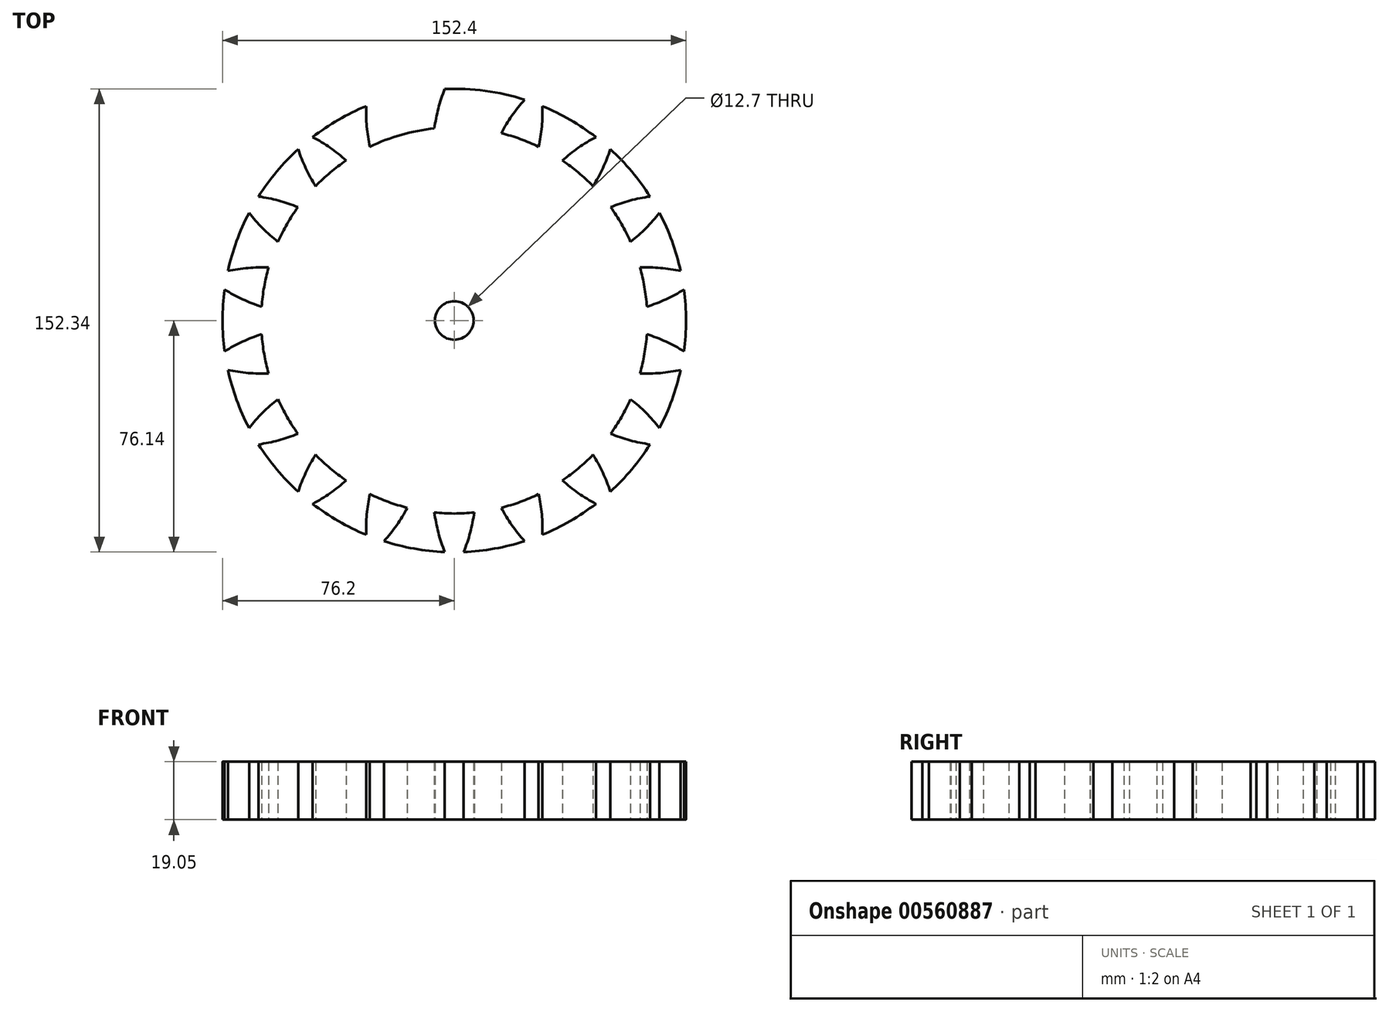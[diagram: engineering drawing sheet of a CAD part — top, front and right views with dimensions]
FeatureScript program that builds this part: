
annotation { "Feature Type Name" : "Feature", "Feature Type Description" : "" }
export const myFeature = defineFeature(function(context is Context, id is Id, definition is map)
    precondition{}
    {
        {
            var Q0;
            Q0=qCreatedBy(makeId("Top.planeOp"),FACE);
            var sketch = newSketch(context, id + "F0", { "sketchPlane" : qUnion([Q0])});
            skCircle(sketch, "E0", {"center": v(0, 0) * mm, "radius": 63.5 * mm});
            skLineSegment(sketch, "E1", {"start": v(0, 0) * mm, "end": v(-81.9, 97.6) * mm, "construction": true});
            skCircle(sketch, "E2", {"center": v(-46.94, 55.94) * mm, "radius": 53.98 * mm, "construction": true});
            skCircle(sketch, "E3", {"center": v(0, 0) * mm, "radius": 76.2 * mm});
            skArc(sketch, "E4", {"start": v(6.55, 63.16) * mm, "mid": v(5.24, 69.76) * mm, "end": v(3.11, 76.14) * mm});
            skArc(sketch, "E5.MirrorCS", {"start": v(-6.55, 63.16) * mm, "mid": v(-5.24, 69.76) * mm, "end": v(-3.11, 76.14) * mm});
            skArc(sketch, "E6", {"start": v(-3.11, 76.14) * mm, "mid": v(0, 76.2) * mm, "end": v(3.11, 76.14) * mm});
            skArc(sketch, "E7.1.0", {"start": v(15.45, 61.6) * mm, "mid": v(18.94, 67.34) * mm, "end": v(23.11, 72.61) * mm});
            skArc(sketch, "E7.1.1", {"start": v(27.76, 57.11) * mm, "mid": v(28.78, 63.76) * mm, "end": v(28.97, 70.48) * mm});
            skArc(sketch, "E7.1.2", {"start": v(23.11, 72.61) * mm, "mid": v(26.06, 71.6) * mm, "end": v(28.97, 70.48) * mm});
            skArc(sketch, "E7.2.0", {"start": v(35.58, 52.6) * mm, "mid": v(40.83, 56.8) * mm, "end": v(46.55, 60.33) * mm});
            skArc(sketch, "E7.2.1", {"start": v(45.62, 44.17) * mm, "mid": v(48.85, 50.07) * mm, "end": v(51.33, 56.32) * mm});
            skArc(sketch, "E7.2.2", {"start": v(46.55, 60.33) * mm, "mid": v(48.98, 58.37) * mm, "end": v(51.33, 56.32) * mm});
            skArc(sketch, "E7.3.0", {"start": v(51.42, 37.25) * mm, "mid": v(57.8, 39.41) * mm, "end": v(64.38, 40.77) * mm});
            skArc(sketch, "E7.3.1", {"start": v(57.97, 25.9) * mm, "mid": v(63.03, 30.34) * mm, "end": v(67.5, 35.37) * mm});
            skArc(sketch, "E7.3.2", {"start": v(64.38, 40.77) * mm, "mid": v(66, 38.1) * mm, "end": v(67.5, 35.37) * mm});
            skArc(sketch, "E7.4.0", {"start": v(61.06, 17.42) * mm, "mid": v(67.79, 17.27) * mm, "end": v(74.44, 16.29) * mm});
            skArc(sketch, "E7.4.1", {"start": v(63.34, 4.52) * mm, "mid": v(69.6, 6.96) * mm, "end": v(75.52, 10.15) * mm});
            skArc(sketch, "E7.4.2", {"start": v(74.44, 16.29) * mm, "mid": v(75.04, 13.23) * mm, "end": v(75.52, 10.15) * mm});
            skArc(sketch, "E7.5.0", {"start": v(63.34, -4.52) * mm, "mid": v(69.6, -6.96) * mm, "end": v(75.52, -10.15) * mm});
            skArc(sketch, "E7.5.1", {"start": v(61.06, -17.42) * mm, "mid": v(67.79, -17.27) * mm, "end": v(74.44, -16.29) * mm});
            skArc(sketch, "E7.5.2", {"start": v(75.52, -10.15) * mm, "mid": v(75.04, -13.23) * mm, "end": v(74.44, -16.29) * mm});
            skArc(sketch, "E7.6.0", {"start": v(57.97, -25.9) * mm, "mid": v(63.03, -30.34) * mm, "end": v(67.5, -35.37) * mm});
            skArc(sketch, "E7.6.1", {"start": v(51.42, -37.25) * mm, "mid": v(57.8, -39.41) * mm, "end": v(64.38, -40.77) * mm});
            skArc(sketch, "E7.6.2", {"start": v(67.5, -35.37) * mm, "mid": v(66, -38.1) * mm, "end": v(64.38, -40.77) * mm});
            skArc(sketch, "E7.7.0", {"start": v(45.62, -44.17) * mm, "mid": v(48.85, -50.07) * mm, "end": v(51.33, -56.32) * mm});
            skArc(sketch, "E7.7.1", {"start": v(35.58, -52.6) * mm, "mid": v(40.83, -56.8) * mm, "end": v(46.55, -60.33) * mm});
            skArc(sketch, "E7.7.2", {"start": v(51.33, -56.32) * mm, "mid": v(48.98, -58.37) * mm, "end": v(46.55, -60.33) * mm});
            skArc(sketch, "E7.8.0", {"start": v(27.76, -57.11) * mm, "mid": v(28.78, -63.76) * mm, "end": v(28.97, -70.48) * mm});
            skArc(sketch, "E7.8.1", {"start": v(15.45, -61.6) * mm, "mid": v(18.94, -67.34) * mm, "end": v(23.11, -72.61) * mm});
            skArc(sketch, "E7.8.2", {"start": v(28.97, -70.48) * mm, "mid": v(26.06, -71.6) * mm, "end": v(23.11, -72.61) * mm});
            skArc(sketch, "E7.9.0", {"start": v(6.55, -63.16) * mm, "mid": v(5.24, -69.76) * mm, "end": v(3.11, -76.14) * mm});
            skArc(sketch, "E7.9.1", {"start": v(-6.55, -63.16) * mm, "mid": v(-5.24, -69.76) * mm, "end": v(-3.11, -76.14) * mm});
            skArc(sketch, "E7.9.2", {"start": v(3.11, -76.14) * mm, "mid": v(0, -76.2) * mm, "end": v(-3.11, -76.14) * mm});
            skArc(sketch, "E7.10.0", {"start": v(-15.45, -61.6) * mm, "mid": v(-18.94, -67.34) * mm, "end": v(-23.11, -72.61) * mm});
            skArc(sketch, "E7.10.1", {"start": v(-27.76, -57.11) * mm, "mid": v(-28.78, -63.76) * mm, "end": v(-28.97, -70.48) * mm});
            skArc(sketch, "E7.10.2", {"start": v(-23.11, -72.61) * mm, "mid": v(-26.06, -71.6) * mm, "end": v(-28.97, -70.48) * mm});
            skArc(sketch, "E7.11.0", {"start": v(-35.58, -52.6) * mm, "mid": v(-40.83, -56.8) * mm, "end": v(-46.55, -60.33) * mm});
            skArc(sketch, "E7.11.1", {"start": v(-45.62, -44.17) * mm, "mid": v(-48.85, -50.07) * mm, "end": v(-51.33, -56.32) * mm});
            skArc(sketch, "E7.11.2", {"start": v(-46.55, -60.33) * mm, "mid": v(-48.98, -58.37) * mm, "end": v(-51.33, -56.32) * mm});
            skArc(sketch, "E7.12.0", {"start": v(-51.42, -37.25) * mm, "mid": v(-57.8, -39.41) * mm, "end": v(-64.38, -40.77) * mm});
            skArc(sketch, "E7.12.1", {"start": v(-57.97, -25.9) * mm, "mid": v(-63.03, -30.34) * mm, "end": v(-67.5, -35.37) * mm});
            skArc(sketch, "E7.12.2", {"start": v(-64.38, -40.77) * mm, "mid": v(-66, -38.1) * mm, "end": v(-67.5, -35.37) * mm});
            skArc(sketch, "E7.13.0", {"start": v(-61.06, -17.42) * mm, "mid": v(-67.79, -17.27) * mm, "end": v(-74.44, -16.29) * mm});
            skArc(sketch, "E7.13.1", {"start": v(-63.34, -4.52) * mm, "mid": v(-69.6, -6.96) * mm, "end": v(-75.52, -10.15) * mm});
            skArc(sketch, "E7.13.2", {"start": v(-74.44, -16.29) * mm, "mid": v(-75.04, -13.23) * mm, "end": v(-75.52, -10.15) * mm});
            skArc(sketch, "E7.14.0", {"start": v(-63.34, 4.52) * mm, "mid": v(-69.6, 6.96) * mm, "end": v(-75.52, 10.15) * mm});
            skArc(sketch, "E7.14.1", {"start": v(-61.06, 17.42) * mm, "mid": v(-67.79, 17.27) * mm, "end": v(-74.44, 16.29) * mm});
            skArc(sketch, "E7.14.2", {"start": v(-75.52, 10.15) * mm, "mid": v(-75.04, 13.23) * mm, "end": v(-74.44, 16.29) * mm});
            skArc(sketch, "E7.15.0", {"start": v(-57.97, 25.9) * mm, "mid": v(-63.03, 30.34) * mm, "end": v(-67.5, 35.37) * mm});
            skArc(sketch, "E7.15.1", {"start": v(-51.42, 37.25) * mm, "mid": v(-57.8, 39.41) * mm, "end": v(-64.38, 40.77) * mm});
            skArc(sketch, "E7.15.2", {"start": v(-67.5, 35.37) * mm, "mid": v(-66, 38.1) * mm, "end": v(-64.38, 40.77) * mm});
            skArc(sketch, "E7.16.0", {"start": v(-45.62, 44.17) * mm, "mid": v(-48.85, 50.07) * mm, "end": v(-51.33, 56.32) * mm});
            skArc(sketch, "E7.16.1", {"start": v(-35.58, 52.6) * mm, "mid": v(-40.83, 56.8) * mm, "end": v(-46.55, 60.33) * mm});
            skArc(sketch, "E7.16.2", {"start": v(-51.33, 56.32) * mm, "mid": v(-48.98, 58.37) * mm, "end": v(-46.55, 60.33) * mm});
            skArc(sketch, "E7.17.0", {"start": v(-27.76, 57.11) * mm, "mid": v(-28.78, 63.76) * mm, "end": v(-28.97, 70.48) * mm});
            skArc(sketch, "E7.17.1", {"start": v(-15.45, 61.6) * mm, "mid": v(-18.94, 67.34) * mm, "end": v(-23.11, 72.61) * mm});
            skArc(sketch, "E7.17.2", {"start": v(-28.97, 70.48) * mm, "mid": v(-26.06, 71.6) * mm, "end": v(-23.11, 72.61) * mm});
            skLineSegment(sketch, "E7.anchor1", {"start": v(0, 0) * mm, "end": v(-6.55, 63.16) * mm, "construction": true});
            skLineSegment(sketch, "E7.anchor2", {"start": v(0, 0) * mm, "end": v(-27.76, 57.11) * mm, "construction": true});
            skCircle(sketch, "E8", {"center": v(0, 0) * mm, "radius": 6.35 * mm});
            skSolve(sketch);
        }
        {
            var Q0;
            {var subQ0=sQuery(id+"F0.wireOp",EDGE,"E7.4.0");Q0=makeQuery(id+"F0.imprint","IMPRINT",FACE,{"disambiguationData":[TD([[makeQuery(id+"F0.imprint","IMPRINT",EDGE,{"derivedFrom":subQ0}),-1.0]])]});}
            var Q1;
            {var subQ0=sQuery(id+"F0.wireOp",EDGE,"E7.3.0");Q1=makeQuery(id+"F0.imprint","IMPRINT",FACE,{"disambiguationData":[TD([[makeQuery(id+"F0.imprint","IMPRINT",EDGE,{"derivedFrom":subQ0}),-1.0]])]});}
            var Q2;
            {var subQ0=sQuery(id+"F0.wireOp",EDGE,"E7.2.0");Q2=makeQuery(id+"F0.imprint","IMPRINT",FACE,{"disambiguationData":[TD([[makeQuery(id+"F0.imprint","IMPRINT",EDGE,{"derivedFrom":subQ0}),-1.0]])]});}
            var Q3;
            {var subQ0=sQuery(id+"F0.wireOp",EDGE,"E7.1.0");Q3=makeQuery(id+"F0.imprint","IMPRINT",FACE,{"disambiguationData":[TD([[makeQuery(id+"F0.imprint","IMPRINT",EDGE,{"derivedFrom":subQ0}),-1.0]])]});}
            var Q4;
            {var subQ0=sQuery(id+"F0.wireOp",EDGE,"E4");Q4=makeQuery(id+"F0.imprint","IMPRINT",FACE,{"disambiguationData":[TD([[makeQuery(id+"F0.imprint","IMPRINT",EDGE,{"derivedFrom":subQ0}),1.0]])]});}
            var Q5;
            {var subQ0=sQuery(id+"F0.wireOp",EDGE,"E7.17.0");Q5=makeQuery(id+"F0.imprint","IMPRINT",FACE,{"disambiguationData":[TD([[makeQuery(id+"F0.imprint","IMPRINT",EDGE,{"derivedFrom":subQ0}),-1.0]])]});}
            var Q6;
            {var subQ0=sQuery(id+"F0.wireOp",EDGE,"E7.16.0");Q6=makeQuery(id+"F0.imprint","IMPRINT",FACE,{"disambiguationData":[TD([[makeQuery(id+"F0.imprint","IMPRINT",EDGE,{"derivedFrom":subQ0}),-1.0]])]});}
            var Q7;
            {var subQ0=sQuery(id+"F0.wireOp",EDGE,"E7.15.0");Q7=makeQuery(id+"F0.imprint","IMPRINT",FACE,{"disambiguationData":[TD([[makeQuery(id+"F0.imprint","IMPRINT",EDGE,{"derivedFrom":subQ0}),-1.0]])]});}
            var Q8;
            {var subQ0=sQuery(id+"F0.wireOp",EDGE,"E7.14.0");Q8=makeQuery(id+"F0.imprint","IMPRINT",FACE,{"disambiguationData":[TD([[makeQuery(id+"F0.imprint","IMPRINT",EDGE,{"derivedFrom":subQ0}),-1.0]])]});}
            var Q9;
            {var subQ0=sQuery(id+"F0.wireOp",EDGE,"E7.13.0");Q9=makeQuery(id+"F0.imprint","IMPRINT",FACE,{"disambiguationData":[TD([[makeQuery(id+"F0.imprint","IMPRINT",EDGE,{"derivedFrom":subQ0}),-1.0]])]});}
            var Q10;
            {var subQ0=sQuery(id+"F0.wireOp",EDGE,"E7.12.0");Q10=makeQuery(id+"F0.imprint","IMPRINT",FACE,{"disambiguationData":[TD([[makeQuery(id+"F0.imprint","IMPRINT",EDGE,{"derivedFrom":subQ0}),-1.0]])]});}
            var Q11;
            {var subQ0=sQuery(id+"F0.wireOp",EDGE,"E7.11.0");Q11=makeQuery(id+"F0.imprint","IMPRINT",FACE,{"disambiguationData":[TD([[makeQuery(id+"F0.imprint","IMPRINT",EDGE,{"derivedFrom":subQ0}),-1.0]])]});}
            var Q12;
            {var subQ0=sQuery(id+"F0.wireOp",EDGE,"E7.10.0");Q12=makeQuery(id+"F0.imprint","IMPRINT",FACE,{"disambiguationData":[TD([[makeQuery(id+"F0.imprint","IMPRINT",EDGE,{"derivedFrom":subQ0}),-1.0]])]});}
            var Q13;
            {var subQ0=sQuery(id+"F0.wireOp",EDGE,"E7.9.0");Q13=makeQuery(id+"F0.imprint","IMPRINT",FACE,{"disambiguationData":[TD([[makeQuery(id+"F0.imprint","IMPRINT",EDGE,{"derivedFrom":subQ0}),-1.0]])]});}
            var Q14;
            {var subQ0=sQuery(id+"F0.wireOp",EDGE,"E7.8.0");Q14=makeQuery(id+"F0.imprint","IMPRINT",FACE,{"disambiguationData":[TD([[makeQuery(id+"F0.imprint","IMPRINT",EDGE,{"derivedFrom":subQ0}),-1.0]])]});}
            var Q15;
            {var subQ0=sQuery(id+"F0.wireOp",EDGE,"E7.7.0");Q15=makeQuery(id+"F0.imprint","IMPRINT",FACE,{"disambiguationData":[TD([[makeQuery(id+"F0.imprint","IMPRINT",EDGE,{"derivedFrom":subQ0}),-1.0]])]});}
            var Q16;
            {var subQ0=sQuery(id+"F0.wireOp",EDGE,"E7.6.0");Q16=makeQuery(id+"F0.imprint","IMPRINT",FACE,{"disambiguationData":[TD([[makeQuery(id+"F0.imprint","IMPRINT",EDGE,{"derivedFrom":subQ0}),-1.0]])]});}
            var Q17;
            {var subQ0=sQuery(id+"F0.wireOp",EDGE,"E7.5.0");Q17=makeQuery(id+"F0.imprint","IMPRINT",FACE,{"disambiguationData":[TD([[makeQuery(id+"F0.imprint","IMPRINT",EDGE,{"derivedFrom":subQ0}),-1.0]])]});}
            var Q18;
            {var subQ0=sQuery(id+"F0.wireOp",EDGE,"E0");var subQ17=makeQuery(id+"F0.imprint","INTERSECT",VERTEX,{"derivedFrom":[subQ0,sQuery(id+"F0.wireOp",EDGE,"E7.4.0")]});Q18=makeQuery(id+"F0.imprint","IMPRINT",FACE,{"disambiguationData":[TD([[makeQuery(id+"F0.imprint","IMPRINT",EDGE,{"disambiguationData":[TD([[subQ17,1.0]])],"derivedFrom":subQ0}),1.0]])]});}
            extrude(context, id + "F1", {"entities" : qUnion([Q0, Q1, Q2, Q3, Q4, Q5, Q6, Q7, Q8, Q9, Q10, Q11, Q12, Q13, Q14, Q15, Q16, Q17, Q18]), "depth" : 19.05 * mm, "offsetDistance" : 25.4 * mm});
        }
    });
